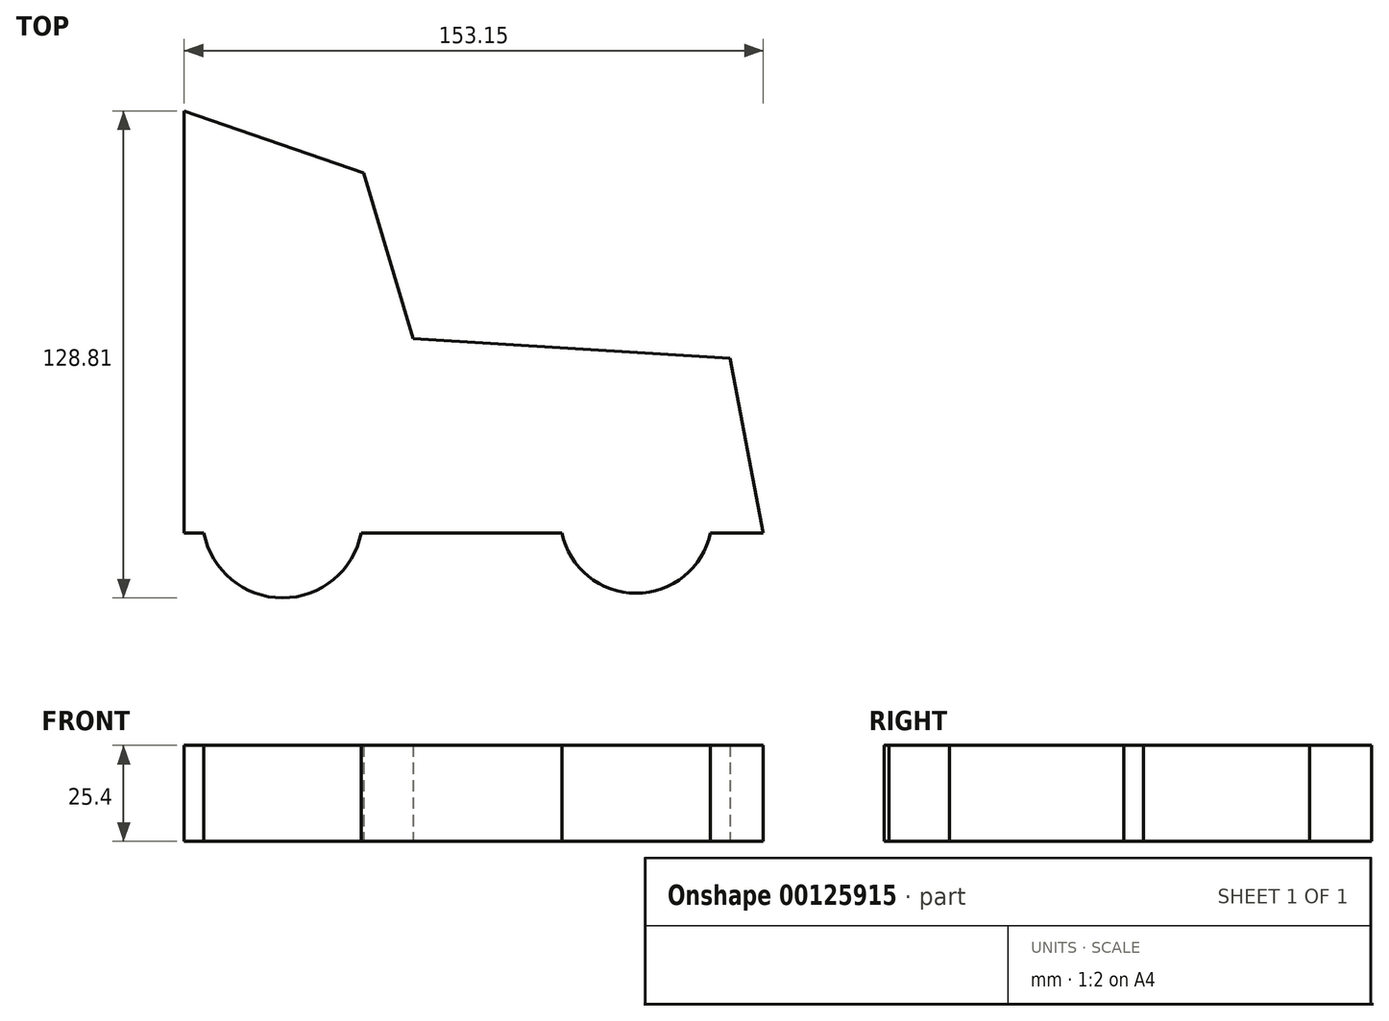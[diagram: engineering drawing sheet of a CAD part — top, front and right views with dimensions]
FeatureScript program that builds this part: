
annotation { "Feature Type Name" : "Feature", "Feature Type Description" : "" }
export const myFeature = defineFeature(function(context is Context, id is Id, definition is map)
    precondition{}
    {
        {
            var Q0;
            Q0=qCreatedBy(makeId("Top.planeOp"),FACE);
            var sketch = newSketch(context, id + "F0", { "sketchPlane" : qUnion([Q0])});
            skLineSegment(sketch, "E0", {"start": v(-75.76, -75.43) * mm, "end": v(77.4, -75.43) * mm});
            skLineSegment(sketch, "E1", {"start": v(77.4, -75.43) * mm, "end": v(68.56, -29.29) * mm});
            skLineSegment(sketch, "E2", {"start": v(68.56, -29.29) * mm, "end": v(-15.22, -24.05) * mm});
            skLineSegment(sketch, "E3", {"start": v(-15.22, -24.05) * mm, "end": v(-28.3, 19.8) * mm});
            skLineSegment(sketch, "E4", {"start": v(-75.76, -75.43) * mm, "end": v(-75.76, 36.16) * mm});
            skLineSegment(sketch, "E5", {"start": v(-75.76, 36.16) * mm, "end": v(-28.3, 19.8) * mm});
            skSolve(sketch);
        }
        {
            var Q0;
            Q0 = qSketchRegion(id + "F0", true);
            extrude(context, id + "F1", {"entities" : qUnion([Q0]), "depth" : 25.4 * mm});
        }
        {
            var Q0;
            Q0=qCreatedBy(makeId("Top.planeOp"),FACE);
            var sketch = newSketch(context, id + "F2", { "sketchPlane" : qUnion([Q0])});
            skCircle(sketch, "E6", {"center": v(-49.77, -71.5) * mm, "radius": 21.15 * mm});
            skCircle(sketch, "E7", {"center": v(43.75, -71.33) * mm, "radius": 20.08 * mm});
            skSolve(sketch);
        }
        {
            var Q0;
            Q0 = qSketchRegion(id + "F2", true);
            extrude(context, id + "F3", {"entities" : qUnion([Q0]), "operationType" : NewBodyOperationType.ADD, "depth" : 25.4 * mm});
        }
    });
